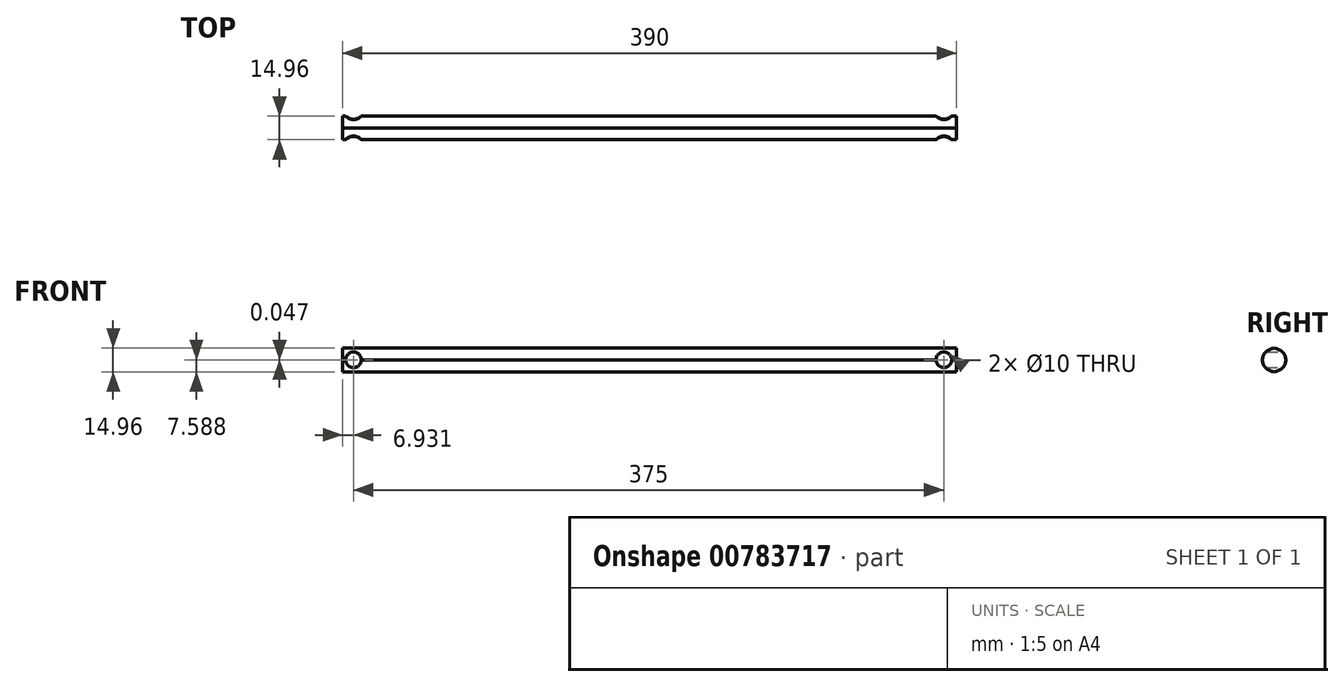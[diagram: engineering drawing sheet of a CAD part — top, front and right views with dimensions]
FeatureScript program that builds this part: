
annotation { "Feature Type Name" : "Feature", "Feature Type Description" : "" }
export const myFeature = defineFeature(function(context is Context, id is Id, definition is map)
    precondition{}
    {
        {
            var Q0;
            Q0=qCreatedBy(makeId("Front.planeOp"),FACE);
            var sketch = newSketch(context, id + "F0", { "sketchPlane" : qUnion([Q0])});
            skLineSegment(sketch, "E0.bottom", {"start": v(-390, 15) * mm, "end": v(0, 15) * mm});
            skLineSegment(sketch, "E0.top", {"start": v(-390, 0) * mm, "end": v(0, 0) * mm});
            skLineSegment(sketch, "E0.left", {"start": v(-390, 15) * mm, "end": v(-390, 0) * mm});
            skLineSegment(sketch, "E0.right", {"start": v(0, 15) * mm, "end": v(0, 0) * mm});
            skSolve(sketch);
        }
        {
            var Q0;
            Q0=makeQuery(id+"F0.imprint","IMPRINT",FACE,{"disambiguationData":[TD([[makeQuery(id+"F0.imprint","IMPRINT",EDGE,{"derivedFrom":sQuery(id+"F0.wireOp",EDGE,"E0.bottom")}),-1.0]])]});
            extrude(context, id + "F1", {"entities" : qUnion([Q0]), "depth" : 15 * mm, "offsetDistance" : 25 * mm});
        }
        {
            var Q0;
            Q0=qCreatedBy(makeId("Front.planeOp"),FACE);
            var sketch = newSketch(context, id + "F2", { "sketchPlane" : qUnion([Q0])});
            skCircle(sketch, "E1", {"center": v(-383.07, 7.6) * mm, "radius": 5 * mm});
            skCircle(sketch, "E2", {"center": v(-8.07, 7.66) * mm, "radius": 5 * mm});
            skSolve(sketch);
        }
        {
            var Q0;
            Q0=qSketchRegion(id+"F2",true);
            extrude(context, id + "F3", {"entities" : qUnion([Q0]), "operationType" : NewBodyOperationType.REMOVE, "depth" : 20 * mm, "offsetDistance" : 25 * mm});
        }
        {
            var Q0;
            Q0=makeQuery(id+"F1.opExtrude","CAP_EDGE",EDGE,{"disambiguationData":[OSD([sQuery(id+"F0.wireOp",EDGE,"E0.bottom")])],"isStart":true});
            var Q1;
            Q1=makeQuery(id+"F1.opExtrude","CAP_EDGE",EDGE,{"disambiguationData":[OSD([sQuery(id+"F0.wireOp",EDGE,"E0.top")])],"isStart":true});
            var Q2;
            Q2=makeQuery(id+"F1.opExtrude","CAP_EDGE",EDGE,{"disambiguationData":[OSD([sQuery(id+"F0.wireOp",EDGE,"E0.bottom")])],"isStart":false});
            var Q3;
            Q3=makeQuery(id+"F1.opExtrude","CAP_EDGE",EDGE,{"disambiguationData":[OSD([sQuery(id+"F0.wireOp",EDGE,"E0.top")])],"isStart":false});
            fillet(context, id + "F4", {"entities" : qUnion([Q0, Q1, Q2, Q3]), "radius" : 8 * mm, "tangentPropagation" : true, "allowEdgeOverflow" : false});
        }
    });
